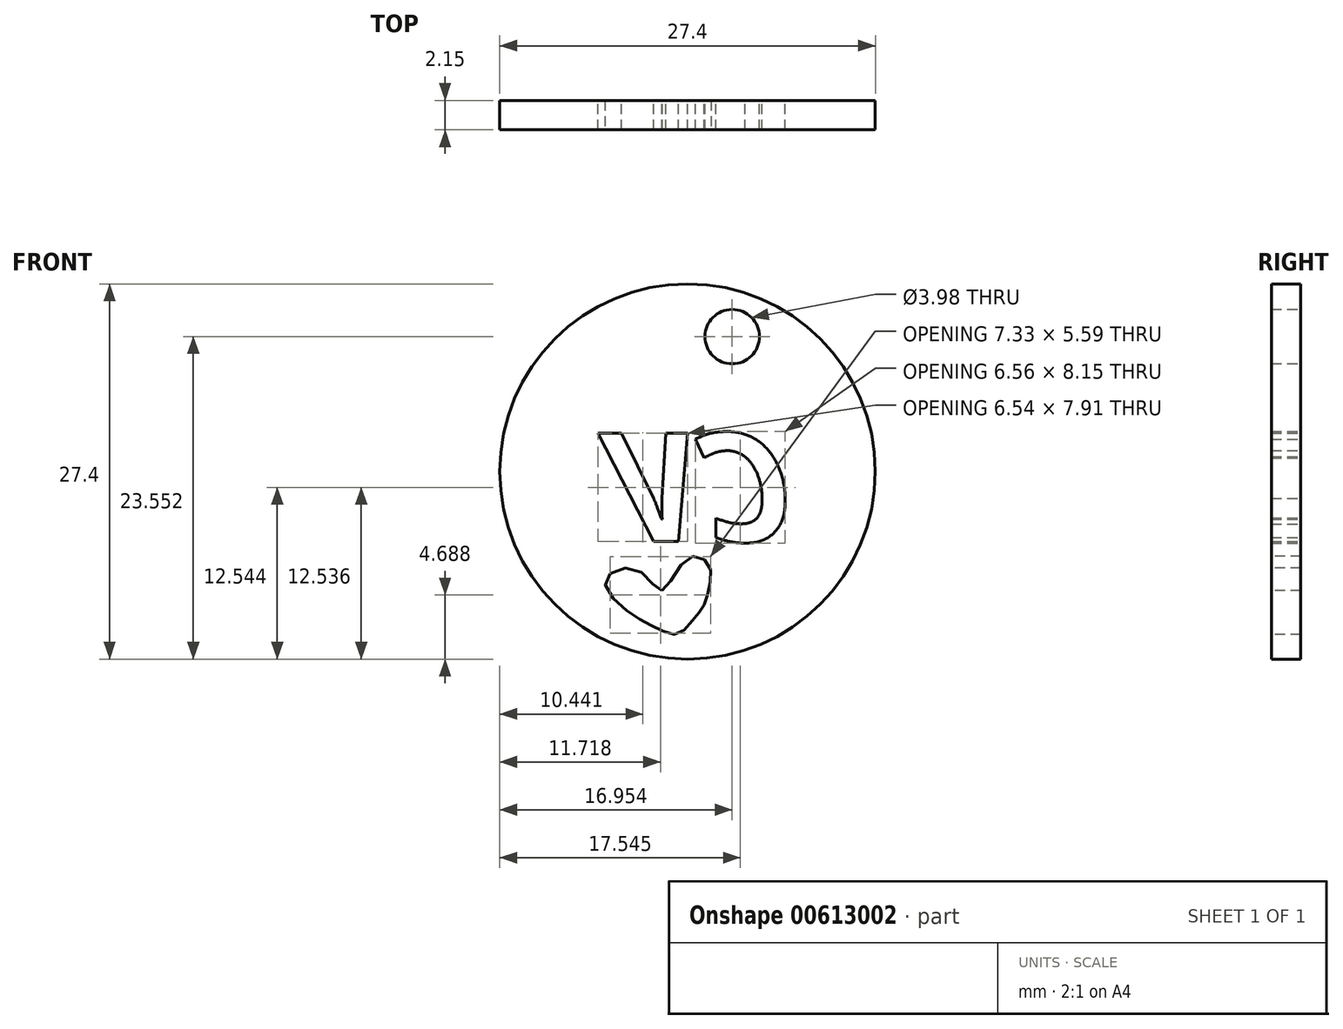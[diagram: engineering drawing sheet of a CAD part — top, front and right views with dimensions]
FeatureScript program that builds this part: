
annotation { "Feature Type Name" : "Feature", "Feature Type Description" : "" }
export const myFeature = defineFeature(function(context is Context, id is Id, definition is map)
    precondition{}
    {
        {
            var Q0;
            Q0=qCreatedBy(makeId("Front.planeOp"),FACE);
            var sketch = newSketch(context, id + "F0", { "sketchPlane" : qUnion([Q0])});
            skCircle(sketch, "E0", {"center": v(-47.33, 45.8) * mm, "radius": 13.7 * mm});
            skPoint(sketch, "E1", {"position": v(-47.6, 59.5) * mm});
            skSolve(sketch);
        }
        {
            var Q0;
            Q0=makeQuery(id+"F0.imprint","IMPRINT",FACE,{"disambiguationData":[TD([[makeQuery(id+"F0.imprint","IMPRINT",EDGE,{"derivedFrom":sQuery(id+"F0.wireOp",EDGE,"E0")}),1.0]])]});
            extrude(context, id + "F1", {"entities" : qUnion([Q0]), "depth" : 2.15 * mm, "offsetDistance" : 25 * mm});
        }
        {
            var Q0;
            Q0=makeQuery(id+"F1.opExtrude","CAP_FACE",FACE,{"disambiguationData":[OSD([sQuery(id+"F0.wireOp",EDGE,"E0")])],"isStart":true});
            var sketch = newSketch(context, id + "F2", { "sketchPlane" : qUnion([Q0])});
            skCircle(sketch, "E2", {"center": v(44.08, 55.66) * mm, "radius": 1.99 * mm});
            skSolve(sketch);
        }
        {
            var Q0;
            Q0=makeQuery(id+"F2.imprint","IMPRINT",FACE,{"disambiguationData":[TD([[makeQuery(id+"F2.imprint","IMPRINT",EDGE,{"derivedFrom":sQuery(id+"F2.wireOp",EDGE,"E2")}),1.0]])]});
            extrude(context, id + "F3", {"entities" : qUnion([Q0]), "operationType" : NewBodyOperationType.REMOVE, "endBound" : BoundingType.UP_TO_NEXT, "oppositeDirection" : true, "depth" : 25 * mm, "offsetDistance" : 25 * mm});
        }
        {
            var Q0;
            Q0=makeQuery(id+"F1.opExtrude","CAP_FACE",FACE,{"disambiguationData":[OSD([sQuery(id+"F0.wireOp",EDGE,"E0")])],"isStart":true});
            var sketch = newSketch(context, id + "F4", { "sketchPlane" : qUnion([Q0])});
            skText(sketch, "E3", { "text": "CV", "fontName": "OpenSans-BoldItalic.ttf"});
            const initialGuessF4  = {"E3": [0.03954, 0.04069, 1, 0, 0.00798]};
            skSetInitialGuess(sketch, initialGuessF4);
            skSolve(sketch);
        }
        {
            var Q0;
            Q0=makeQuery(id+"F4.imprint","IMPRINT",FACE,{"disambiguationData":[TD([[makeQuery(id+"F4.imprint","IMPRINT",EDGE,{"derivedFrom":sQuery(id+"F4.wireOp",EDGE,"E3.sketch_text.stroke-18")}),-1.0]])]});
            var Q1;
            Q1 = qSketchRegion(id + "F4", true);
            extrude(context, id + "F5", {"entities" : qUnion([Q0, Q1]), "operationType" : NewBodyOperationType.REMOVE, "endBound" : BoundingType.UP_TO_NEXT, "oppositeDirection" : true, "depth" : 25 * mm, "offsetDistance" : 25 * mm});
        }
        {
            var Q0;
            Q0=qCreatedBy(makeId("Front.planeOp"),FACE);
            var sketch = newSketch(context, id + "F6", { "sketchPlane" : qUnion([Q0])});
            skFitSpline(sketch, "E4", {"points": [v(-49.2, 37.13) * mm, v(-50.98, 38.63) * mm, v(-53.32, 37.88) * mm, v(-51.64, 35.54) * mm, v(-49.67, 34.42) * mm, v(-48.08, 33.95) * mm, v(-46.87, 35.07) * mm, v(-46.21, 35.91) * mm, v(-45.74, 37.41) * mm, v(-45.84, 39.1) * mm, v(-47.33, 39.47) * mm, v(-49.2, 37.13) * mm]});
            skSolve(sketch);
        }
        {
            var Q0;
            Q0=makeQuery(id+"F6.imprint","IMPRINT",FACE,{"disambiguationData":[TD([[makeQuery(id+"F6.imprint","IMPRINT",EDGE,{"derivedFrom":sQuery(id+"F6.wireOp",EDGE,"E4")}),1.0]])]});
            extrude(context, id + "F7", {"entities" : qUnion([Q0]), "operationType" : NewBodyOperationType.REMOVE, "endBound" : BoundingType.UP_TO_NEXT, "depth" : 25 * mm, "offsetDistance" : 25 * mm});
        }
    });
